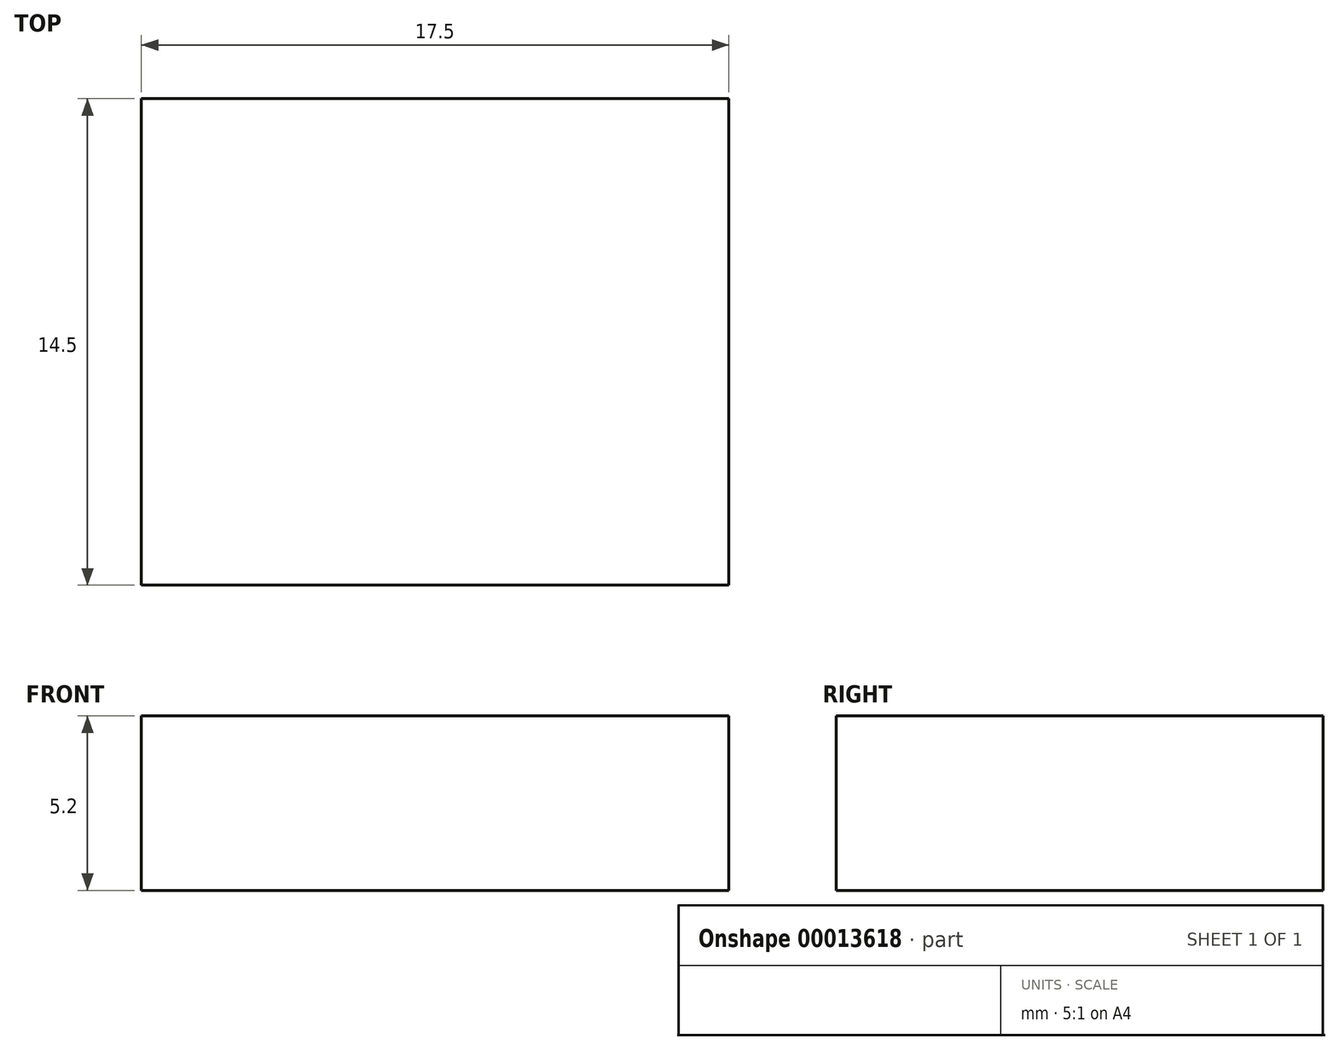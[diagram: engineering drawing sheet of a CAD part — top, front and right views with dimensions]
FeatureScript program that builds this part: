
annotation { "Feature Type Name" : "Feature", "Feature Type Description" : "" }
export const myFeature = defineFeature(function(context is Context, id is Id, definition is map)
    precondition{}
    {
        {
            var Q0;
            Q0=qCreatedBy(makeId("Top.planeOp"),FACE);
            var sketch = newSketch(context, id + "F0", { "sketchPlane" : qUnion([Q0])});
            skLineSegment(sketch, "E0.bottom", {"start": v(-14.5, 6.64) * mm, "end": v(3, 6.64) * mm});
            skLineSegment(sketch, "E0.top", {"start": v(-14.5, -7.86) * mm, "end": v(3, -7.86) * mm});
            skLineSegment(sketch, "E0.left", {"start": v(-14.5, 6.64) * mm, "end": v(-14.5, -7.86) * mm});
            skLineSegment(sketch, "E0.right", {"start": v(3, 6.64) * mm, "end": v(3, -7.86) * mm});
            skLineSegment(sketch, "E1.left", {"start": v(-14.5, 6.64) * mm, "end": v(-14.5, -4.36) * mm});
            skSolve(sketch);
        }
        {
            var Q0;
            Q0=makeQuery(id+"F0.imprint","IMPRINT",FACE,{"disambiguationData":[TD([[makeQuery(id+"F0.imprint","IMPRINT",EDGE,{"derivedFrom":sQuery(id+"F0.wireOp",EDGE,"E0.bottom")}),-1.0]])]});
            extrude(context, id + "F1", {"entities" : qUnion([Q0]), "depth" : 5.2 * mm});
        }
    });
